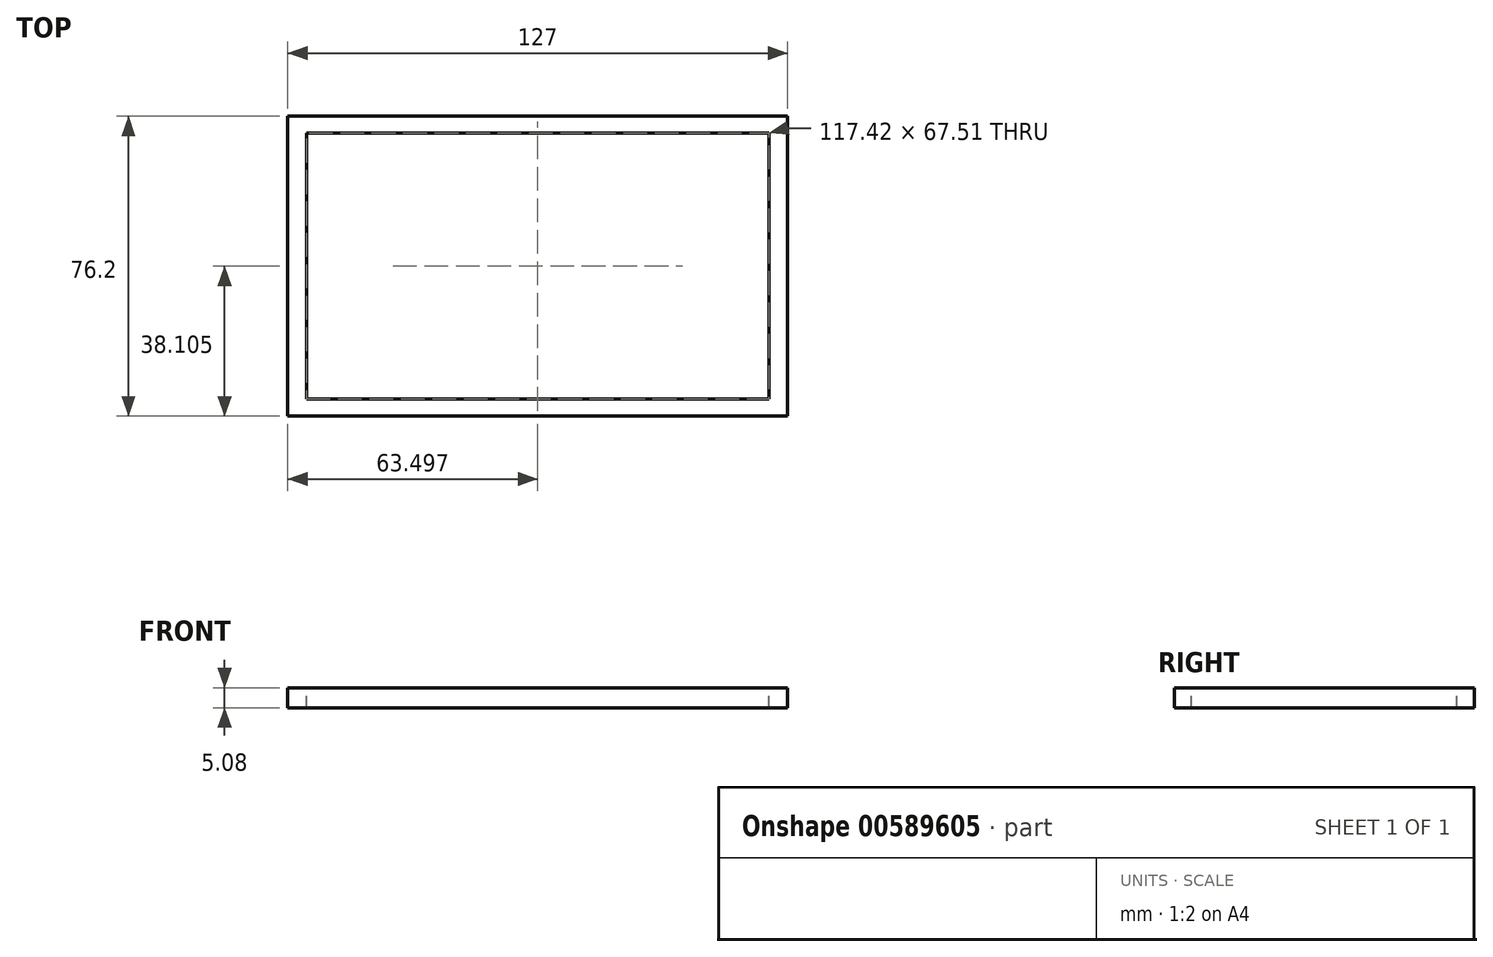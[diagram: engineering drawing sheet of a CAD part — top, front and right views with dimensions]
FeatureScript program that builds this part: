
annotation { "Feature Type Name" : "Feature", "Feature Type Description" : "" }
export const myFeature = defineFeature(function(context is Context, id is Id, definition is map)
    precondition{}
    {
        {
            var Q0;
            Q0=qCreatedBy(makeId("Top.planeOp"),FACE);
            var sketch = newSketch(context, id + "F0", { "sketchPlane" : qUnion([Q0])});
            skLineSegment(sketch, "E0.bottom", {"start": v(-62.5, 62.62) * mm, "end": v(64.5, 62.62) * mm});
            skLineSegment(sketch, "E0.top", {"start": v(-62.5, -13.58) * mm, "end": v(64.5, -13.58) * mm});
            skLineSegment(sketch, "E0.left", {"start": v(-62.5, 62.62) * mm, "end": v(-62.5, -13.58) * mm});
            skLineSegment(sketch, "E0.right", {"start": v(64.5, 62.62) * mm, "end": v(64.5, -13.58) * mm});
            skSolve(sketch);
        }
        {
            var Q0;
            Q0=makeQuery(id+"F0.imprint","IMPRINT",FACE,{"disambiguationData":[TD([[makeQuery(id+"F0.imprint","IMPRINT",EDGE,{"derivedFrom":sQuery(id+"F0.wireOp",EDGE,"E0.bottom")}),-1.0]])]});
            extrude(context, id + "F1", {"entities" : qUnion([Q0]), "depth" : 5.08 * mm, "offsetDistance" : 25.4 * mm});
        }
        {
            var Q0;
            Q0=makeQuery(id+"F1.opExtrude","CAP_FACE",FACE,{"disambiguationData":[OSD([sQuery(id+"F0.wireOp",EDGE,"E0.bottom"),sQuery(id+"F0.wireOp",EDGE,"E0.top"),sQuery(id+"F0.wireOp",EDGE,"E0.left"),sQuery(id+"F0.wireOp",EDGE,"E0.right")])],"isStart":false});
            var sketch = newSketch(context, id + "F2", { "sketchPlane" : qUnion([Q0])});
            skLineSegment(sketch, "E1.bottom", {"start": v(-57.7, 58.28) * mm, "end": v(59.72, 58.28) * mm});
            skLineSegment(sketch, "E1.top", {"start": v(-57.7, -9.23) * mm, "end": v(59.72, -9.23) * mm});
            skLineSegment(sketch, "E1.left", {"start": v(-57.7, 58.28) * mm, "end": v(-57.7, -9.23) * mm});
            skLineSegment(sketch, "E1.right", {"start": v(59.72, 58.28) * mm, "end": v(59.72, -9.23) * mm});
            skPoint(sketch, "E1.middle", {"position": v(1, 24.52) * mm});
            skPoint(sketch, "E1.middle.positionSnap0", {"position": v(1, 62.62) * mm});
            skPoint(sketch, "E1.middle.positionSnap1", {"position": v(-62.5, 24.52) * mm});
            skPoint(sketch, "E1.centerSnap0", {"position": v(1, 62.62) * mm});
            skPoint(sketch, "E1.centerSnap1", {"position": v(-62.5, 24.52) * mm});
            skSolve(sketch);
        }
        {
            var Q0;
            Q0=makeQuery(id+"F2.imprint","IMPRINT",FACE,{"disambiguationData":[TD([[makeQuery(id+"F2.imprint","IMPRINT",EDGE,{"derivedFrom":sQuery(id+"F2.wireOp",EDGE,"E1.bottom")}),-1.0]])]});
            extrude(context, id + "F3", {"entities" : qUnion([Q0]), "operationType" : NewBodyOperationType.REMOVE, "oppositeDirection" : true, "depth" : 25.4 * mm, "offsetDistance" : 25.4 * mm});
        }
    });
